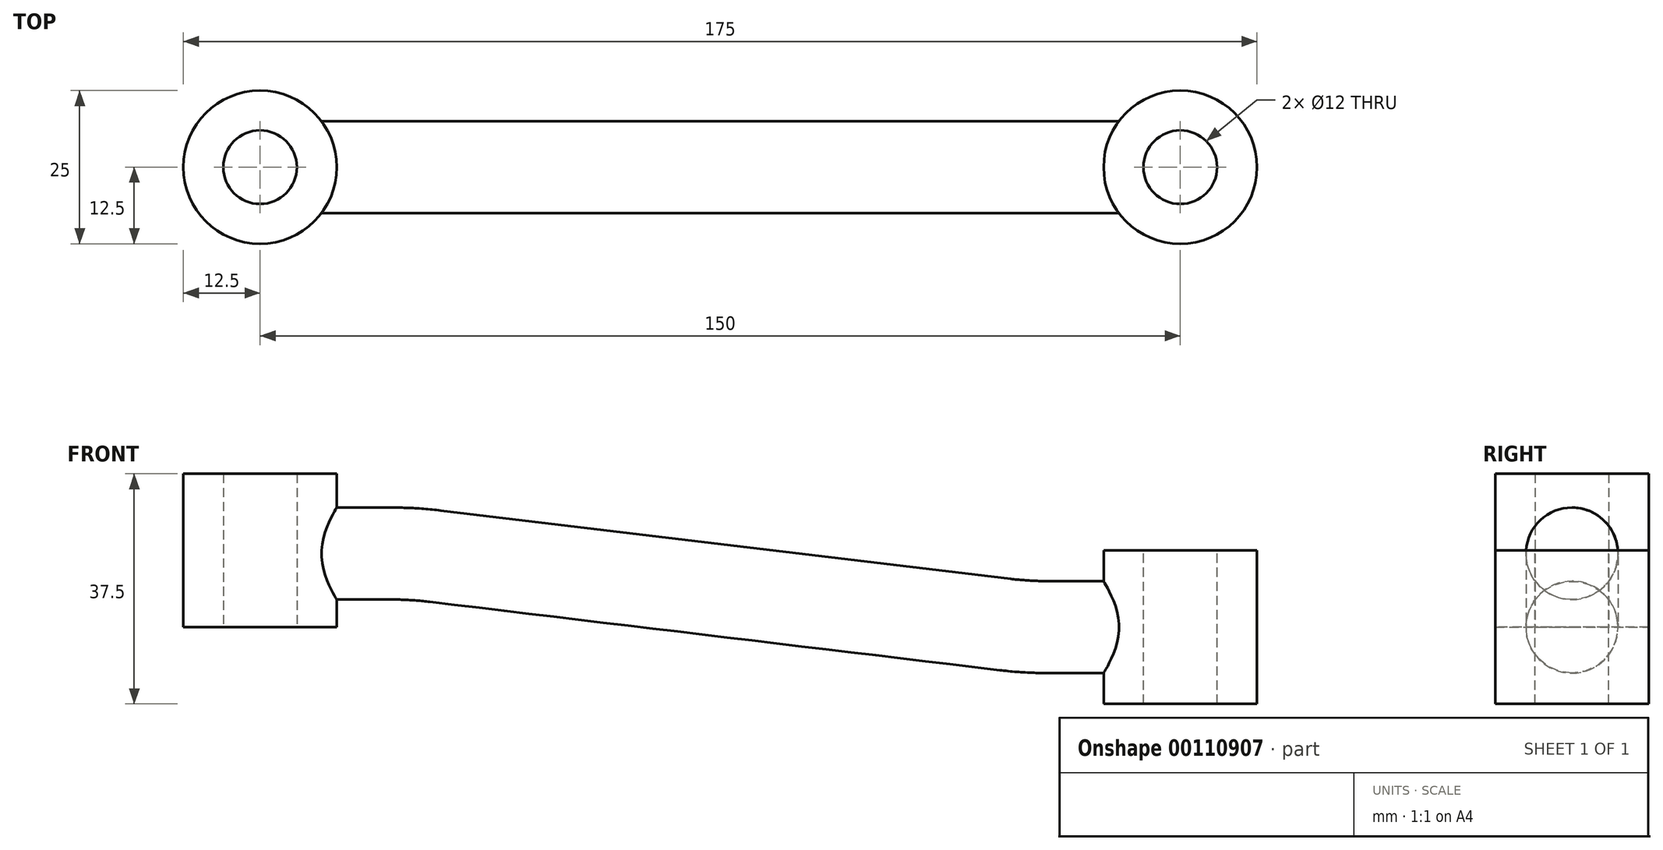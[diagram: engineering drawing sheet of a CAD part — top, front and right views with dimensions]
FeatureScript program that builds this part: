
annotation { "Feature Type Name" : "Feature", "Feature Type Description" : "" }
export const myFeature = defineFeature(function(context is Context, id is Id, definition is map)
    precondition{}
    {
        {
            var Q0;
            Q0=qCreatedBy(makeId("Top.planeOp"),FACE);
            var sketch = newSketch(context, id + "F0", { "sketchPlane" : qUnion([Q0])});
            skCircle(sketch, "E0", {"center": v(0, 0) * mm, "radius": 6 * mm});
            skCircle(sketch, "E1", {"center": v(0, 0) * mm, "radius": 12.5 * mm});
            skCircle(sketch, "E2", {"center": v(150, 0) * mm, "radius": 6 * mm});
            skCircle(sketch, "E3", {"center": v(150, 0) * mm, "radius": 12.5 * mm});
            skLineSegment(sketch, "E4", {"start": v(0, 0) * mm, "end": v(150, 0) * mm, "construction": true});
            skSolve(sketch);
        }
        {
            var Q0;
            Q0=qCreatedBy(makeId("Front.planeOp"),FACE);
            var sketch = newSketch(context, id + "F1", { "sketchPlane" : qUnion([Q0])});
            skLineSegment(sketch, "E5", {"start": v(0, 0) * mm, "end": v(0, 12) * mm, "construction": true});
            skLineSegment(sketch, "E6", {"start": v(0, 12) * mm, "end": v(0, 25) * mm, "construction": true});
            skLineSegment(sketch, "E7", {"start": v(0, 12) * mm, "end": v(21.41, 12) * mm});
            skLineSegment(sketch, "E8", {"start": v(128.59, 0) * mm, "end": v(150, 0) * mm});
            skLineSegment(sketch, "E9", {"start": v(28.56, 11.57) * mm, "end": v(121.44, 0.43) * mm});
            skPoint(sketch, "E10.visualSharp", {"position": v(25, 12) * mm});
            skArc(sketch, "E10.filletArc", {"start": v(28.56, 11.57) * mm, "mid": v(25, 11.9) * mm, "end": v(21.41, 12) * mm});
            skPoint(sketch, "E11.visualSharp", {"position": v(125, 0) * mm});
            skArc(sketch, "E11.filletArc", {"start": v(121.44, 0.43) * mm, "mid": v(125, 0.1) * mm, "end": v(128.59, 0) * mm});
            skSolve(sketch);
        }
        {
            var Q0;
            Q0=makeQuery(id+"F0.imprint","IMPRINT",FACE,{"disambiguationData":[TD([[makeQuery(id+"F0.imprint","IMPRINT",EDGE,{"derivedFrom":sQuery(id+"F0.wireOp",EDGE,"E0")}),-1.0]])]});
            extrude(context, id + "F2", {"entities" : qUnion([Q0]), "depth" : 25 * mm});
        }
        {
            var Q0;
            Q0=makeQuery(id+"F0.imprint","IMPRINT",FACE,{"disambiguationData":[TD([[makeQuery(id+"F0.imprint","IMPRINT",EDGE,{"derivedFrom":sQuery(id+"F0.wireOp",EDGE,"E2")}),-1.0]])]});
            extrude(context, id + "F3", {"entities" : qUnion([Q0]), "operationType" : NewBodyOperationType.ADD, "endBound" : BoundingType.SYMMETRIC, "oppositeDirection" : true, "depth" : 25 * mm});
        }
        {
            var Q0;
            Q0=qCreatedBy(makeId("Right.planeOp"),FACE);
            var sketch = newSketch(context, id + "F4", { "sketchPlane" : qUnion([Q0])});
            skLineSegment(sketch, "E12", {"start": v(0, 0) * mm, "end": v(0, 12) * mm, "construction": true});
            skCircle(sketch, "E13", {"center": v(0, 12) * mm, "radius": 7.5 * mm});
            skSolve(sketch);
        }
        {
            var Q0;
            Q0 = qSketchRegion(id + "F4", true);
            var Q1;
            Q1=sQuery(id+"F4.wireOp",EDGE,"E13");
            var Q2;
            Q2=sQuery(id+"F1.wireOp",EDGE,"E7");
            var Q3;
            Q3=sQuery(id+"F1.wireOp",EDGE,"E10.filletArc");
            var Q4;
            Q4=sQuery(id+"F1.wireOp",EDGE,"E9");
            var Q5;
            Q5=sQuery(id+"F1.wireOp",EDGE,"E11.filletArc");
            var Q6;
            Q6=sQuery(id+"F1.wireOp",EDGE,"E8");
            sweep(context, id + "F5", {"operationType" : NewBodyOperationType.ADD, "profiles" : qUnion([Q0]), "surfaceProfiles" : qUnion([Q1]), "path" : qUnion([Q2, Q3, Q4, Q5, Q6])});
        }
        {
            var Q0;
            Q0=qCreatedBy(makeId("Top.planeOp"),FACE);
            var sketch = newSketch(context, id + "F6", { "sketchPlane" : qUnion([Q0])});
            skCircle(sketch, "E14", {"center": v(0, 0) * mm, "radius": 6 * mm});
            skCircle(sketch, "E15", {"center": v(150, 0) * mm, "radius": 6 * mm});
            skSolve(sketch);
        }
        {
            var Q0;
            Q0 = qSketchRegion(id + "F6", true);
            extrude(context, id + "F7", {"entities" : qUnion([Q0]), "operationType" : NewBodyOperationType.REMOVE, "endBound" : BoundingType.SYMMETRIC, "depth" : 50 * mm});
        }
    });
